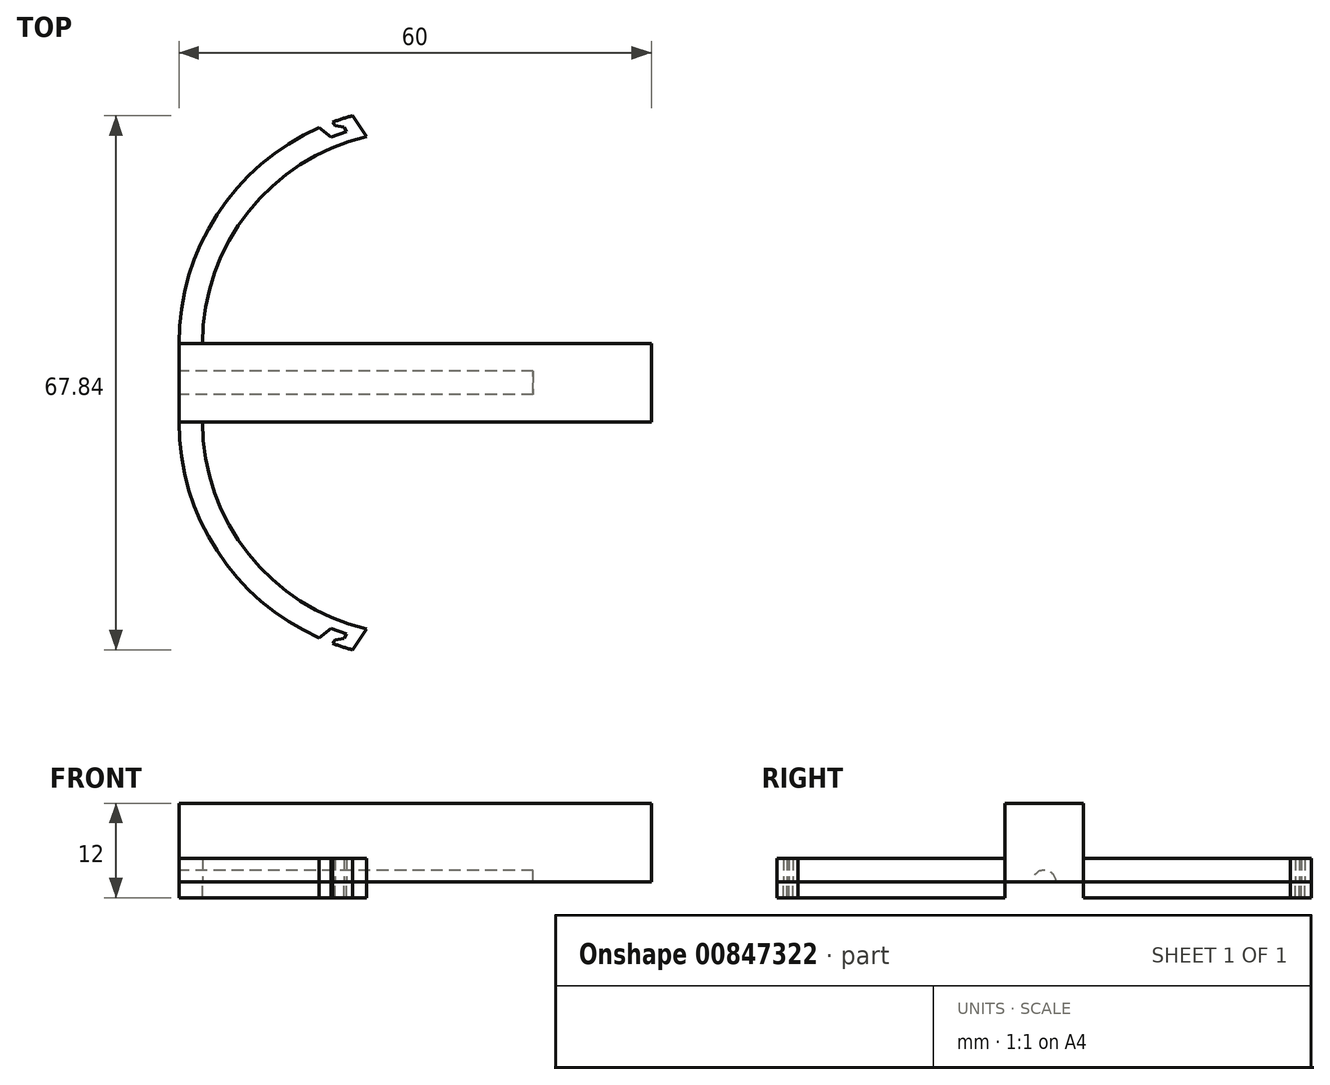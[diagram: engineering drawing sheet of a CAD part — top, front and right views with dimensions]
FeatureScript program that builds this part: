
annotation { "Feature Type Name" : "Feature", "Feature Type Description" : "" }
export const myFeature = defineFeature(function(context is Context, id is Id, definition is map)
    precondition{}
    {
        {
            var Q0;
            Q0=qCreatedBy(makeId("Top.planeOp"),FACE);
            var sketch = newSketch(context, id + "F0", { "sketchPlane" : qUnion([Q0])});
            skLineSegment(sketch, "E0", {"start": v(0, 0) * mm, "end": v(0, 5) * mm});
            skLineSegment(sketch, "E1", {"start": v(0, 5) * mm, "end": v(60, 5) * mm});
            skLineSegment(sketch, "E2", {"start": v(60, 5) * mm, "end": v(60, 0) * mm});
            skLineSegment(sketch, "E3.MirrorCS", {"start": v(60, -5) * mm, "end": v(60, 0) * mm});
            skLineSegment(sketch, "E4.MirrorCS", {"start": v(0, 0) * mm, "end": v(0, -5) * mm});
            skLineSegment(sketch, "E5.MirrorCS", {"start": v(0, -5) * mm, "end": v(60, -5) * mm});
            skArc(sketch, "E6.MirrorCS", {"start": v(3, -5) * mm, "mid": v(8.83, -21.76) * mm, "end": v(23.81, -31.28) * mm});
            skArc(sketch, "E7.MirrorCS", {"start": v(0, -5) * mm, "mid": v(4.84, -21.34) * mm, "end": v(17.8, -32.4) * mm});
            skLineSegment(sketch, "E8", {"start": v(0, 0) * mm, "end": v(60, 0) * mm, "construction": true});
            skLineSegment(sketch, "E9.0", {"start": v(45, 0) * mm, "end": v(45, -5) * mm, "construction": true});
            skLineSegment(sketch, "E10", {"start": v(23.81, -31.28) * mm, "end": v(22.03, -33.92) * mm});
            skLineSegment(sketch, "E11", {"start": v(19.53, -33.11) * mm, "end": v(19.82, -32.7) * mm});
            skLineSegment(sketch, "E12", {"start": v(19.82, -32.7) * mm, "end": v(21, -32.45) * mm});
            skLineSegment(sketch, "E13", {"start": v(21, -32.45) * mm, "end": v(21.28, -31.9) * mm});
            skLineSegment(sketch, "E14", {"start": v(21.28, -31.9) * mm, "end": v(19.32, -31.2) * mm});
            skLineSegment(sketch, "E15", {"start": v(19.32, -31.2) * mm, "end": v(17.8, -32.4) * mm});
            skArc(sketch, "E16.trimOffspring", {"start": v(19.53, -33.11) * mm, "mid": v(20.77, -33.54) * mm, "end": v(22.03, -33.92) * mm});
            skLineSegment(sketch, "E17.MirrorCS", {"start": v(21, 32.45) * mm, "end": v(21.28, 31.9) * mm});
            skArc(sketch, "E18.MirrorCS", {"start": v(19.53, 33.11) * mm, "mid": v(20.77, 33.54) * mm, "end": v(22.03, 33.92) * mm});
            skLineSegment(sketch, "E19.MirrorCS", {"start": v(21.28, 31.9) * mm, "end": v(19.32, 31.2) * mm});
            skLineSegment(sketch, "E20.MirrorCS", {"start": v(19.82, 32.7) * mm, "end": v(21, 32.45) * mm});
            skLineSegment(sketch, "E21.MirrorCS", {"start": v(19.53, 33.11) * mm, "end": v(19.82, 32.7) * mm});
            skLineSegment(sketch, "E22.MirrorCS", {"start": v(23.81, 31.28) * mm, "end": v(22.03, 33.92) * mm});
            skLineSegment(sketch, "E23.MirrorCS", {"start": v(19.32, 31.2) * mm, "end": v(17.8, 32.4) * mm});
            skArc(sketch, "E24.MirrorCS", {"start": v(3, 5) * mm, "mid": v(8.83, 21.76) * mm, "end": v(23.81, 31.28) * mm});
            skArc(sketch, "E25.MirrorCS", {"start": v(0, 5) * mm, "mid": v(4.84, 21.34) * mm, "end": v(17.8, 32.4) * mm});
            skSolve(sketch);
        }
        {
            var Q0;
            {var subQ1=sQuery(id+"F0.wireOp",EDGE,"E6.MirrorCS");Q0=makeQuery(id+"F0.imprint","IMPRINT",FACE,{"disambiguationData":[TD([[makeQuery(id+"F0.imprint","IMPRINT",EDGE,{"derivedFrom":subQ1}),-1.0]])]});}
            var Q1;
            Q1=makeQuery(id+"F0.imprint","IMPRINT",FACE,{"disambiguationData":[TD([[makeQuery(id+"F0.imprint","IMPRINT",EDGE,{"derivedFrom":sQuery(id+"F0.wireOp",EDGE,"E17.MirrorCS")}),1.0]])]});
            extrude(context, id + "F1", {"entities" : qUnion([Q0, Q1]), "depth" : 3 * mm, "offsetDistance" : 25 * mm});
        }
        {
            var Q0;
            {var subQ3=sQuery(id+"F0.wireOp",EDGE,"E0");Q0=makeQuery(id+"F0.imprint","IMPRINT",FACE,{"disambiguationData":[TD([[makeQuery(id+"F0.imprint","IMPRINT",EDGE,{"derivedFrom":subQ3}),-1.0]])]});}
            extrude(context, id + "F2", {"entities" : qUnion([Q0]), "depth" : 10 * mm, "offsetDistance" : 25 * mm});
        }
        {
            var Q0;
            Q0=makeQuery(id+"F0.imprint","IMPRINT",FACE,{"disambiguationData":[TD([[makeQuery(id+"F0.imprint","IMPRINT",EDGE,{"derivedFrom":sQuery(id+"F0.wireOp",EDGE,"E17.MirrorCS")}),1.0]])]});
            var Q1;
            {var subQ1=sQuery(id+"F0.wireOp",EDGE,"E6.MirrorCS");Q1=makeQuery(id+"F0.imprint","IMPRINT",FACE,{"disambiguationData":[TD([[makeQuery(id+"F0.imprint","IMPRINT",EDGE,{"derivedFrom":subQ1}),-1.0]])]});}
            extrude(context, id + "F3", {"entities" : qUnion([Q0, Q1]), "oppositeDirection" : true, "depth" : 2 * mm, "offsetDistance" : 25 * mm});
        }
        {
            var Q0;
            Q0=makeQuery(id+"F2.opExtrude","SWEPT_FACE",FACE,{"disambiguationData":[OSD([sQuery(id+"F0.wireOp",EDGE,"E0"),sQuery(id+"F0.wireOp",EDGE,"E4.MirrorCS")])]});
            var sketch = newSketch(context, id + "F4", { "sketchPlane" : qUnion([Q0])});
            skCircle(sketch, "E26", {"center": v(0, 0) * mm, "radius": 1.5 * mm});
            skSolve(sketch);
        }
        {
            var Q0;
            {var subQ0=sQuery(id+"F4.wireOp",EDGE,"E26");var subQ1=makeQuery(id+"F2.opExtrude","CAP_EDGE",EDGE,{"disambiguationData":[OSD([sQuery(id+"F0.wireOp",EDGE,"E0"),sQuery(id+"F0.wireOp",EDGE,"E4.MirrorCS")])],"isStart":true});var subQ2=makeQuery(id+"F4.imprint","INTERSECT",VERTEX,{"disambiguationData":[OD(0.0)],"derivedFrom":[subQ1,subQ0]});Q0=makeQuery(id+"F4.imprint","IMPRINT",FACE,{"disambiguationData":[TD([[makeQuery(id+"F4.imprint","IMPRINT",EDGE,{"disambiguationData":[TD([[subQ2,1.0]])],"derivedFrom":subQ0}),1.0]])]});}
            var Q1;
            {var subQ0=sQuery(id+"F4.wireOp",EDGE,"E26");var subQ1=makeQuery(id+"F2.opExtrude","CAP_EDGE",EDGE,{"disambiguationData":[OSD([sQuery(id+"F0.wireOp",EDGE,"E0"),sQuery(id+"F0.wireOp",EDGE,"E4.MirrorCS")])],"isStart":true});var subQ2=makeQuery(id+"F4.imprint","INTERSECT",VERTEX,{"disambiguationData":[OD(0.0)],"derivedFrom":[subQ1,subQ0]});Q1=makeQuery(id+"F4.imprint","IMPRINT",FACE,{"disambiguationData":[TD([[makeQuery(id+"F4.imprint","IMPRINT",EDGE,{"disambiguationData":[TD([[subQ2,-1.0]])],"derivedFrom":subQ0}),1.0]])]});}
            extrude(context, id + "F5", {"entities" : qUnion([Q0, Q1]), "operationType" : NewBodyOperationType.REMOVE, "oppositeDirection" : true, "depth" : 45 * mm, "offsetDistance" : 25 * mm});
        }
    });
